FCSTD DOCUMENT  (FreeCAD 0.16R)
Label: Mk8para
License: All rights reserved
LicenseURL: http://en.wikipedia.org/wiki/All_rights_reserved
objects: Sketcher::SketchObject×1
note: 1 computed .brp shape members not serialized (recipe doc carries the construction recipe); baked Part::Feature solids carry a one-line shape summary decoded from their .brp

FEATURE [Sketcher::SketchObject] Sketch
  sketch-geometry (37):
    g0: Circle CenterX=-406.785 CenterY=335 CenterZ=0 NormalX=0 NormalY=0 NormalZ=1 Radius=335
    g1: Circle CenterX=566.553 CenterY=335 CenterZ=0 NormalX=0 NormalY=0 NormalZ=1 Radius=335
    g2: Circle CenterX=0 CenterY=283.759 CenterZ=0 NormalX=0 NormalY=0 NormalZ=1 Radius=19
    g3: Circle CenterX=325.843 CenterY=891.974 CenterZ=0 NormalX=0 NormalY=0 NormalZ=1 Radius=11.1
    g4: LineSegment StartX=566.553 StartY=335 StartZ=0 EndX=498.121 EndY=490.007 EndZ=0
    g5: LineSegment StartX=0 StartY=283.759 StartZ=0 EndX=-133.289 EndY=634.271 EndZ=0
    g6: Circle [constr] CenterX=0 CenterY=283.759 CenterZ=0 NormalX=0 NormalY=0 NormalZ=1 Radius=127
    g7: LineSegment StartX=588.994 StartY=209.886 StartZ=0 EndX=331.913 EndY=792.209 EndZ=0
    g8: LineSegment [constr] StartX=566.553 StartY=335 StartZ=0 EndX=566.553 EndY=0 EndZ=0
    g9: LineSegment [constr] StartX=588.994 StartY=209.886 StartZ=0 EndX=681.653 EndY=0 EndZ=0
    g10: LineSegment [constr] StartX=329.882 StartY=882.826 StartZ=0 EndX=296.379 EndY=872.698 EndZ=0
    g11: Circle [constr] CenterX=296.379 CenterY=872.698 CenterZ=0 NormalX=0 NormalY=0 NormalZ=1 Radius=19
    g12: Circle [constr] CenterX=312.13 CenterY=837.02 CenterZ=0 NormalX=0 NormalY=0 NormalZ=1 Radius=8
    g13: Circle [constr] CenterX=335.554 CenterY=783.961 CenterZ=0 NormalX=0 NormalY=0 NormalZ=1 Radius=50
    g14: Circle [constr] CenterX=358.575 CenterY=731.816 CenterZ=0 NormalX=0 NormalY=0 NormalZ=1 Radius=7
    g15: LineSegment [constr] StartX=-406.785 StartY=335 StartZ=0 EndX=566.553 EndY=335 EndZ=0
    g16: LineSegment StartX=-406.785 StartY=335 StartZ=0 EndX=-98.6841 EndY=543.27 EndZ=0
    g17: LineSegment StartX=-98.6841 StartY=543.27 StartZ=0 EndX=325.007 EndY=807.853 EndZ=0
    g18: LineSegment StartX=0 StartY=283.759 StartZ=0 EndX=339.413 EndY=775.221 EndZ=0
    g19: LineSegment [constr] StartX=566.553 StartY=0 StartZ=0 EndX=681.653 EndY=0 EndZ=0
    g20: LineSegment [constr] StartX=0 StartY=283.759 StartZ=0 EndX=325.843 EndY=891.974 EndZ=0
    g21: LineSegment [constr] StartX=-406.785 StartY=335 StartZ=0 EndX=0 EndY=283.759 EndZ=0
    g22: LineSegment [constr] StartX=325.843 StartY=891.974 StartZ=0 EndX=329.882 EndY=882.826 EndZ=0
    g23: Circle [constr] CenterX=306.476 CenterY=849.828 CenterZ=0 NormalX=0 NormalY=0 NormalZ=1 Radius=6
    g24: LineSegment StartX=-151.102 StartY=640.882 StartZ=0 EndX=-17.8129 EndY=290.369 EndZ=0
    g25: LineSegment [constr] StartX=-98.6841 StartY=543.27 StartZ=0 EndX=-134.191 EndY=529.724 EndZ=0
    g26: LineSegment StartX=4.65737 StartY=265.338 StartZ=0 EndX=333.52 EndY=741.524 EndZ=0
    g27: LineSegment StartX=-18.8759 StartY=281.591 StartZ=0 EndX=319.966 EndY=772.226 EndZ=0
    g28: LineSegment StartX=-81.7198 StartY=538.891 StartZ=0 EndX=313.908 EndY=785.949 EndZ=0
    g29: LineSegment StartX=-90.922 StartY=563.09 StartZ=0 EndX=303.544 EndY=809.423 EndZ=0
    g30: LineSegment StartX=8.91955 StartY=300.535 StartZ=0 EndX=-124.369 EndY=651.047 EndZ=0
    g31: LineSegment StartX=332.742 StartY=837.375 StartZ=0 EndX=297.979 EndY=822.028 EndZ=0
    g32: LineSegment StartX=297.979 StartY=822.028 StartZ=0 EndX=338.366 EndY=730.546 EndZ=0
    g33: LineSegment StartX=338.366 StartY=730.546 StartZ=0 EndX=373.129 EndY=745.893 EndZ=0
    g34: LineSegment StartX=373.129 StartY=745.893 StartZ=0 EndX=332.742 EndY=837.375 EndZ=0
    g35: LineSegment [constr] StartX=-110.528 StartY=534.184 StartZ=0 EndX=-126.837 EndY=518.995 EndZ=0
    g36: LineSegment [constr] StartX=355.748 StartY=738.22 StartZ=0 EndX=566.553 EndY=335 EndZ=0
  constraints (107):
    c: Radius(g0) = 335
    c: Equal(g0,g1)
    c: Radius(g2) = 19
    c: Tangent(g1,g-1)
    c: Tangent(g0,g-1)
    c: Radius(g3) = 11.1
    c: Distance(g2,g3) = 690
    c: Coincident(g4,g1)
    c: Coincident(g5,g2)
    c: Radius(g6) = 127
    c: Coincident(g6,g2)
    c: Distance(g2,g0) = 410
    c: Parallel(g7,g4)
    c: Distance(g7,g4) = 30
    c: Coincident(g8,g1)
    c: Vertical(g8)
    c: Coincident(g9,g7)
    c: Parallel(g9,g7)
    c: PointOnObject(g10,g7)
    c: Coincident(g11,g10)
    c: Radius(g12) = 8
    c: PointOnObject(g12,g7)
    c: PointOnObject(g13,g7)
    c: Tangent(g13,g12)
    c: Radius(g14) = 7
    c: PointOnObject(g14,g7)
    c: Tangent(g14,g13)
    c: Coincident(g15,g0)
    c: Coincident(g15,g1)
    c: Coincident(g16,g0)
    c: PointOnObject(g16,g5)
    c: Coincident(g17,g16)
    c: PointOnObject(g17,g7)
    c: Coincident(g18,g2)
    c: PointOnObject(g18,g7)
    c: PointOnObject(g19,g8)
    c: PointOnObject(g19,g9)
    c: Horizontal(g19)
    c: Coincident(g8,g19)
    c: PointOnObject(g8,g-1)
    c: Distance(g5) = 375
    c: Coincident(g20,g2)
    c: Distance(g10) = 35
    c: Coincident(g21,g0)
    c: Coincident(g21,g2)
    c: PointOnObject(g2,g-2)
    c: Angle(g7,g10) = 1.44862
    c: Coincident(g22,g10)
    c: Coincident(g20,g22)
    c: Coincident(g3,g20)
    c: Distance(g22) = 10
    c: Parallel(g22,g7)
    c: Radius(g13) = 50
    c: Radius(g11) = 19
    c: PointOnObject(g23,g7)
    c: Tangent(g23,g12)
    c: Tangent(g23,g11)
    c: Parallel(g24,g5)
    c: Distance(g24,g5) = 14.3
    c: PointOnObject(g9,g-1)
    c: PointOnObject(g25,g16)
    c: PointOnObject(g25,g0)
    c: PointOnObject(g24,g2)
    c: Parallel(g17,g29)
    c: Parallel(g29,g28)
    c: Parallel(g27,g26)
    c: Parallel(g26,g18)
    c: Distance(g26,g18) = 14.3
    c: Distance(g27,g18) = 14.3
    c: PointOnObject(g26,g2)
    c: PointOnObject(g27,g2)
    c: Distance(g28,g17) = 12.7
    c: Distance(g29,g17) = 12.7
    c: Parallel(g30,g5)
    c: Distance(g30,g5) = 14.3
    c: PointOnObject(g29,g30)
    c: PointOnObject(g28,g30)
    c: Coincident(g31,g32)
    c: Coincident(g32,g33)
    c: Coincident(g33,g34)
    c: Coincident(g34,g31)
    c: Parallel(g32,g7)
    c: Symmetric(g31,g31,g7)
    c: Symmetric(g33,g32,g7)
    c: Distance(g33,g7) = 19
    c: Tangent(g33,g13)
    c: Tangent(g31,g13)
    c: PointOnObject(g26,g32)
    c: PointOnObject(g29,g32)
    c: Equal(g30,g24)
    c: Equal(g24,g5)
    c: PointOnObject(g30,g2)
    c: PointOnObject(g25,g5)
    c: PointOnObject(g35,g24)
    c: PointOnObject(g35,g0)
    c: PointOnObject(g36,g14)
    c: Coincident(g36,g1)
    c: PointOnObject(g36,g7)
    c: Distance(g36) = 455
    c: Radius(g23) = 6
    c: Angle(g20,g21) = 1.93732
    c: Angle(g20,g7) = 0.907568
    c: Angle(g20,g5) = 0.855208
    c: Distance(g26,g32) = 12
    c: PointOnObject(g27,g32)
    c: PointOnObject(g28,g32)
    c: Distance(g27,g28) = 15
